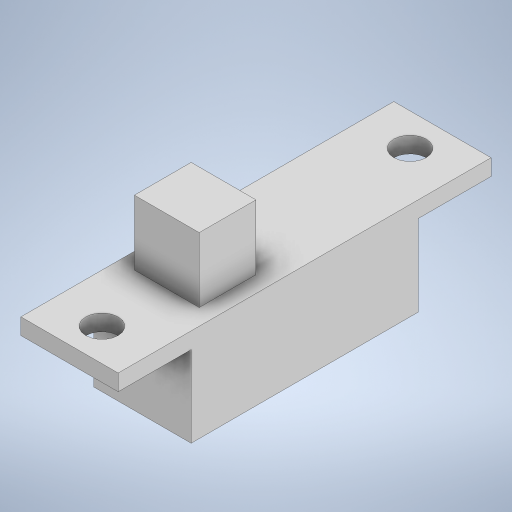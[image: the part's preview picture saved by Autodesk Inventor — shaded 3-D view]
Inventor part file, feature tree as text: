
AUTODESK INVENTOR PART (.ipt)
format: ipt  version: 2024.2 (Build 282272000, 272)  size: 245,760 bytes
history: native  units: mm
features: extrude x3, sketch x3
ambient origin geometry x8: Origin, YZ Plane, XZ Plane, XY Plane, X Axis, Y Axis, Z Axis, Center Point
bodies: Solid1 (feature_tree)
feature tree (6):
  extrude  "Extrusion1"  Depth=23.0mm
  extrude  "Extrusion2"  Depth=2.0mm
  extrude  "Extrusion3"  Depth=4.0mm
  sketch  "Sketch1"  dims[d0=6.0mm d1=23.0mm]
  sketch  "Sketch2"  dims[d2=2.0mm d3=2.0mm]
  sketch  "Sketch3"  dims[d4=19.0mm d5=2.0mm d6=3.0mm d7=1.0mm d8=0.0mm d9=14.0mm d10=4.5mm d11=5.0mm d12=0.0mm d13=4.0mm d14=3.5mm d15=1.0mm d16=6.0mm d17=4.0mm d18=0.0mm]
